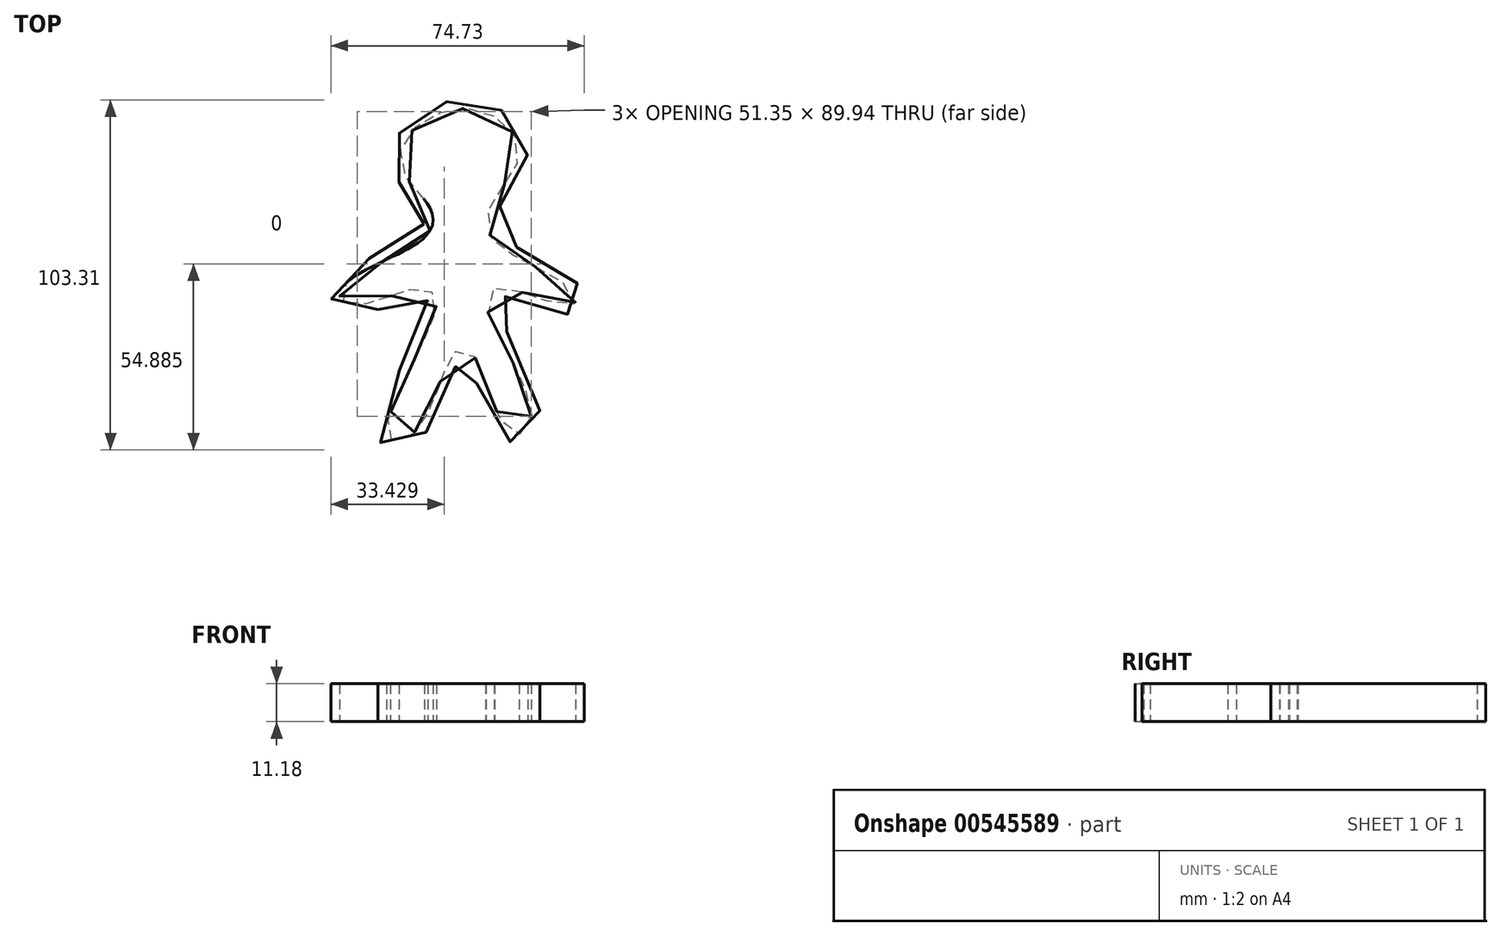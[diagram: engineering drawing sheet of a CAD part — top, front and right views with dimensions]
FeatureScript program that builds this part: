
annotation { "Feature Type Name" : "Feature", "Feature Type Description" : "" }
export const myFeature = defineFeature(function(context is Context, id is Id, definition is map)
    precondition{}
    {
        {
            var Q0;
            Q0=qCreatedBy(makeId("Top.planeOp"),FACE);
            var sketch = newSketch(context, id + "F0", { "sketchPlane" : qUnion([Q0])});
            skFitSpline(sketch, "E0", {"points": [v(-21.06, 26.55) * mm, v(-30.23, 42.14) * mm, v(-22.28, 59.26) * mm, v(0, 61.1) * mm, v(9.2, 44.9) * mm, v(0, 25.63) * mm, v(24.8, 8.2) * mm, v(22.66, 0) * mm, v(0, 4.85) * mm, v(13.18, -30.3) * mm, v(3.09, -37.04) * mm, v(-9.45, -12.88) * mm, v(-21.99, -36.73) * mm, v(-34.53, -36.12) * mm, v(-20.15, 4.25) * mm, v(-42.78, 0) * mm, v(-47.37, 9.14) * mm, v(-21.06, 26.55) * mm]});
            skSolve(sketch);
        }
        {
            var Q0;
            Q0=makeQuery(id+"F0.imprint","IMPRINT",FACE,{"disambiguationData":[TD([[makeQuery(id+"F0.imprint","IMPRINT",EDGE,{"derivedFrom":sQuery(id+"F0.wireOp",EDGE,"E0")}),-1.0]])]});
            extrude(context, id + "F1", {"entities" : qUnion([Q0]), "depth" : 11.18 * mm, "offsetDistance" : 25.4 * mm});
        }
        {
            var Q0;
            Q0=makeQuery(id+"F1.opExtrude","CAP_FACE",FACE,{"disambiguationData":[OSD([sQuery(id+"F0.wireOp",EDGE,"E0")])],"isStart":false});
            var Q1;
            Q1=makeQuery(id+"F1.opExtrude","CAP_FACE",FACE,{"disambiguationData":[OSD([sQuery(id+"F0.wireOp",EDGE,"E0")])],"isStart":true});
            shell(context, id + "F2", {"entities" : qUnion([Q0, Q1]), "thickness" : 2.54 * mm});
        }
    });
